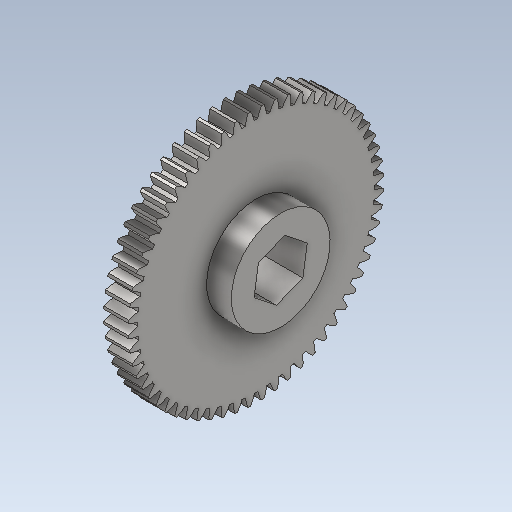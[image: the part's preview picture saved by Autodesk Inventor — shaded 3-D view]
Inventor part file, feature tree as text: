
AUTODESK INVENTOR PART (.ipt)
format: ipt  version: 2023 (Build 270158000, 158)  size: 497,152 bytes
history: native  units: in
note: dims shown in document units (in); Inventor stores cm internally (conversion verified against a paired STEP export)
features: other x3, sketch x2
ambient origin geometry x8: Origin, YZ Plane, XZ Plane, XY Plane, X Axis, Y Axis, Z Axis, Center Point
bodies: Solid1 (feature_tree)
feature tree (5):
  other  "CH-1-01-60T_Idler.ipt"
  other  "Solid1::CH-1-01-60T_Idler.ipt"
  other  "TaggingFeature1"
  sketch  "Sketch3"  dims[d0=0.3937in]
  sketch  "Sketch4"
